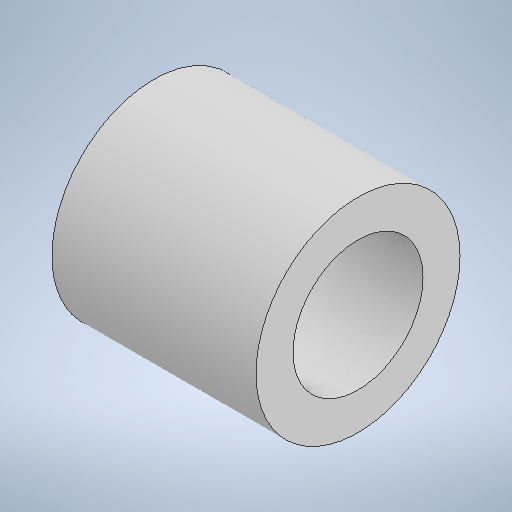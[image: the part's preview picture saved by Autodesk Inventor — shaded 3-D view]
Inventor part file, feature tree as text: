
AUTODESK INVENTOR PART (.ipt)
format: ipt  version: 2025.1 (Build 291241020, 241B)  size: 225,280 bytes
history: native  units: in
note: dims shown in document units (in); Inventor stores cm internally (conversion verified against a paired STEP export)
features: extrude x2, sketch x2, projected_geometry x1
ambient origin geometry x8: Origin, YZ Plane, XZ Plane, XY Plane, X Axis, Y Axis, Z Axis, Center Point
bodies: Solid1 (feature_tree)
feature tree (5):
  extrude  "Extrusion1"  Depth=0.8in
  extrude  "Extrusion2"  Depth=0.07in TaperAngle=0.0deg
  sketch  "Sketch1"  dims[d0=0.51in d1=0.8in]
  sketch  "Sketch2"  dims[d2=0.73in d3=0.0in d4=0.07in d5=0.0in]
  projected_geometry  "Projected Loop1"
